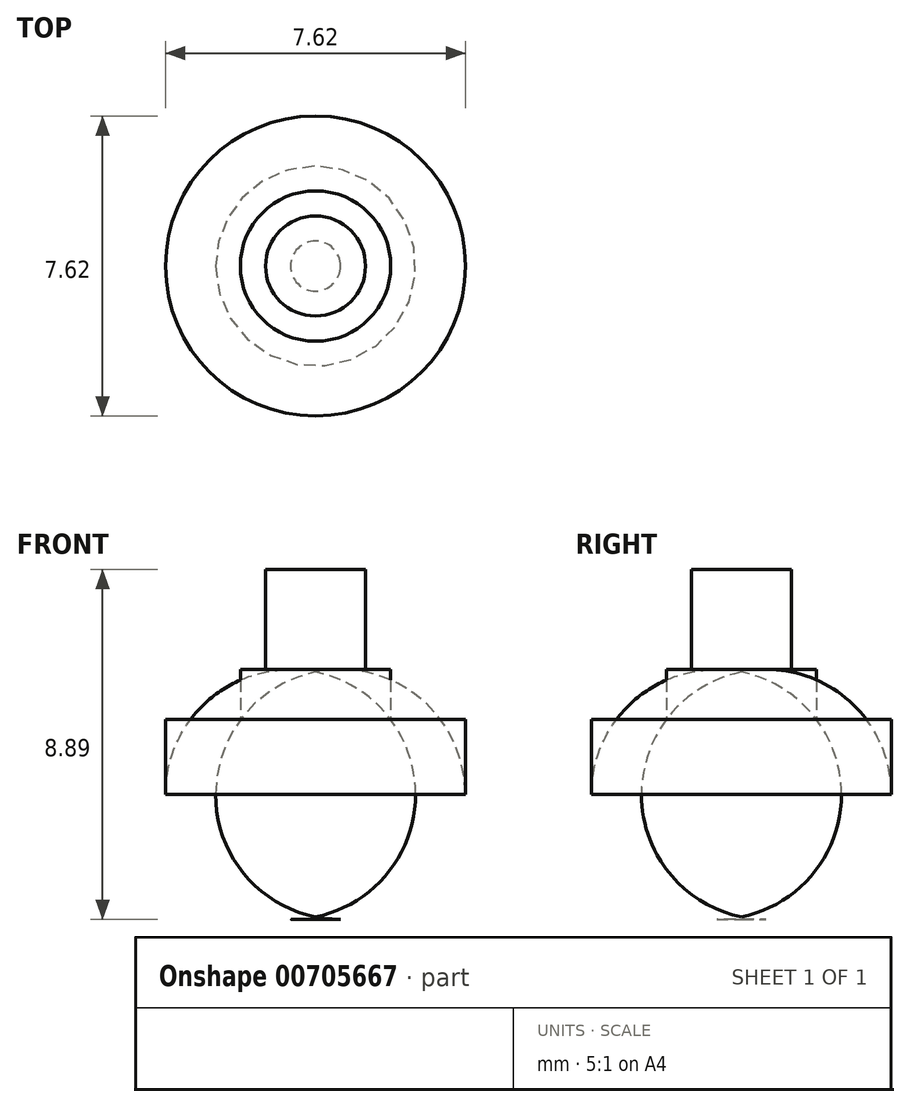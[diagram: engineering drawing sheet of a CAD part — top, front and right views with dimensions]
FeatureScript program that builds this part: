
annotation { "Feature Type Name" : "Feature", "Feature Type Description" : "" }
export const myFeature = defineFeature(function(context is Context, id is Id, definition is map)
    precondition{}
    {
        {
            var Q0;
            Q0=qCreatedBy(makeId("Top.planeOp"),FACE);
            var sketch = newSketch(context, id + "F0", { "sketchPlane" : qUnion([Q0])});
            skCircle(sketch, "E0", {"center": v(0, 0) * mm, "radius": 3.81 * mm});
            skSolve(sketch);
        }
        {
            var Q0;
            Q0 = qSketchRegion(id + "F0", true);
            extrude(context, id + "F1", {"entities" : qUnion([Q0]), "depth" : 5.08 * mm, "offsetDistance" : 25.4 * mm});
        }
        {
            var Q0;
            Q0=makeQuery(id+"F1.opExtrude","CAP_EDGE",EDGE,{"disambiguationData":[OSD([sQuery(id+"F0.wireOp",EDGE,"E0")])],"isStart":true});
            fillet(context, id + "F2", {"entities" : qUnion([Q0]), "radius" : 3.17 * mm, "tangentPropagation" : true, "allowEdgeOverflow" : false});
        }
        {
            var Q0;
            Q0=makeQuery(id+"F1.opExtrude","CAP_FACE",FACE,{"disambiguationData":[OSD([sQuery(id+"F0.wireOp",EDGE,"E0")])],"isStart":false});
            var sketch = newSketch(context, id + "F3", { "sketchPlane" : qUnion([Q0])});
            skCircle(sketch, "E1", {"center": v(0, 0) * mm, "radius": 1.27 * mm});
            skSolve(sketch);
        }
        {
            var Q0;
            Q0 = qSketchRegion(id + "F3", true);
            extrude(context, id + "F4", {"entities" : qUnion([Q0]), "operationType" : NewBodyOperationType.ADD, "depth" : 3.8 * mm, "offsetDistance" : 25.4 * mm});
        }
        {
            var Q0;
            Q0=makeQuery(id+"F1.opExtrude","CAP_FACE",FACE,{"disambiguationData":[OSD([sQuery(id+"F0.wireOp",EDGE,"E0")])],"isStart":false});
            var sketch = newSketch(context, id + "F5", { "sketchPlane" : qUnion([Q0])});
            skCircle(sketch, "E2", {"center": v(0, 0) * mm, "radius": 1.9 * mm});
            skSolve(sketch);
        }
        {
            var Q0;
            Q0 = qSketchRegion(id + "F5", true);
            extrude(context, id + "F6", {"entities" : qUnion([Q0]), "operationType" : NewBodyOperationType.ADD, "depth" : 1.27 * mm, "offsetDistance" : 25.4 * mm});
        }
    });
